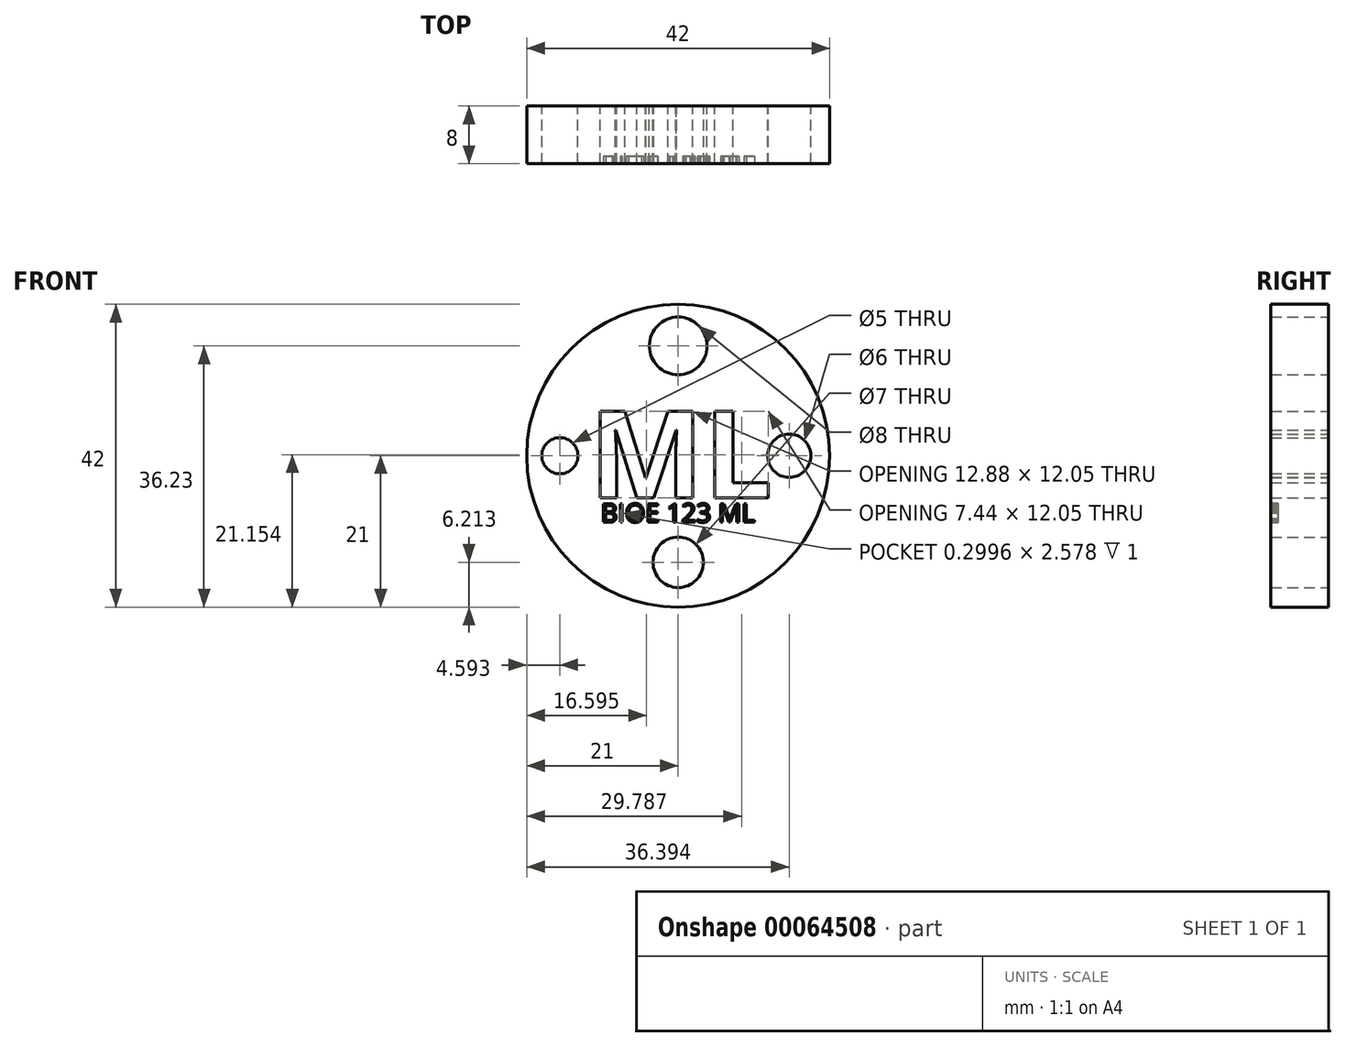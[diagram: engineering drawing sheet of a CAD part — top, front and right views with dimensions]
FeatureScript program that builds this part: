
annotation { "Feature Type Name" : "Feature", "Feature Type Description" : "" }
export const myFeature = defineFeature(function(context is Context, id is Id, definition is map)
    precondition{}
    {
        {
            var Q0;
            Q0=qCreatedBy(makeId("Front.planeOp"),FACE);
            var sketch = newSketch(context, id + "F0", { "sketchPlane" : qUnion([Q0])});
            skCircle(sketch, "E0", {"center": v(0, 0) * mm, "radius": 21 * mm});
            skSolve(sketch);
        }
        {
            var Q0;
            Q0=qCreatedBy(makeId("Front.planeOp"),FACE);
            var sketch = newSketch(context, id + "F1", { "sketchPlane" : qUnion([Q0])});
            skText(sketch, "E1", { "text": "ML", "fontName": "OpenSans-Bold.ttf"});
            const initialGuessF1  = {"E1": [-0.01236, -0.00587, 1, 0, 0.01215]};
            skSetInitialGuess(sketch, initialGuessF1);
            skSolve(sketch);
        }
        {
            var Q0;
            Q0=qCreatedBy(makeId("Front.planeOp"),FACE);
            var sketch = newSketch(context, id + "F2", { "sketchPlane" : qUnion([Q0])});
            skCircle(sketch, "E2", {"center": v(0, 15.23) * mm, "radius": 4 * mm});
            skCircle(sketch, "E3", {"center": v(0, -14.79) * mm, "radius": 3.5 * mm});
            skCircle(sketch, "E4", {"center": v(15.4, 0) * mm, "radius": 3 * mm});
            skCircle(sketch, "E5", {"center": v(-16.4, 0) * mm, "radius": 2.5 * mm});
            skSolve(sketch);
        }
        {
            var Q0;
            Q0=makeQuery(id+"F0.imprint","IMPRINT",FACE,{"disambiguationData":[TD([[makeQuery(id+"F0.imprint","IMPRINT",EDGE,{"derivedFrom":sQuery(id+"F0.wireOp",EDGE,"E0")}),1.0]])]});
            extrude(context, id + "F3", {"entities" : qUnion([Q0]), "depth" : 8 * mm});
        }
        {
            var Q0;
            Q0 = qSketchRegion(id + "F1", true);
            extrude(context, id + "F4", {"entities" : qUnion([Q0]), "operationType" : NewBodyOperationType.REMOVE, "depth" : 8 * mm});
        }
        {
            var Q0;
            Q0 = qSketchRegion(id + "F2", true);
            extrude(context, id + "F5", {"entities" : qUnion([Q0]), "operationType" : NewBodyOperationType.REMOVE, "depth" : 8 * mm});
        }
        {
            var Q0;
            Q0=makeQuery(id+"F3.opExtrude","CAP_FACE",FACE,{"disambiguationData":[OSD([sQuery(id+"F0.wireOp",EDGE,"E0")])],"isStart":false});
            var sketch = newSketch(context, id + "F6", { "sketchPlane" : qUnion([Q0])});
            skText(sketch, "E6", { "text": "BIOE 123 ML", "fontName": "OpenSans-Regular.ttf"});
            const initialGuessF6  = {"E6": [-0.01074, -0.00923, 1, 0, 0.0026]};
            skSetInitialGuess(sketch, initialGuessF6);
            skSolve(sketch);
        }
        {
            var Q0;
            Q0 = qSketchRegion(id + "F6", true);
            extrude(context, id + "F7", {"entities" : qUnion([Q0]), "operationType" : NewBodyOperationType.REMOVE, "oppositeDirection" : true, "depth" : 1 * mm});
        }
    });
